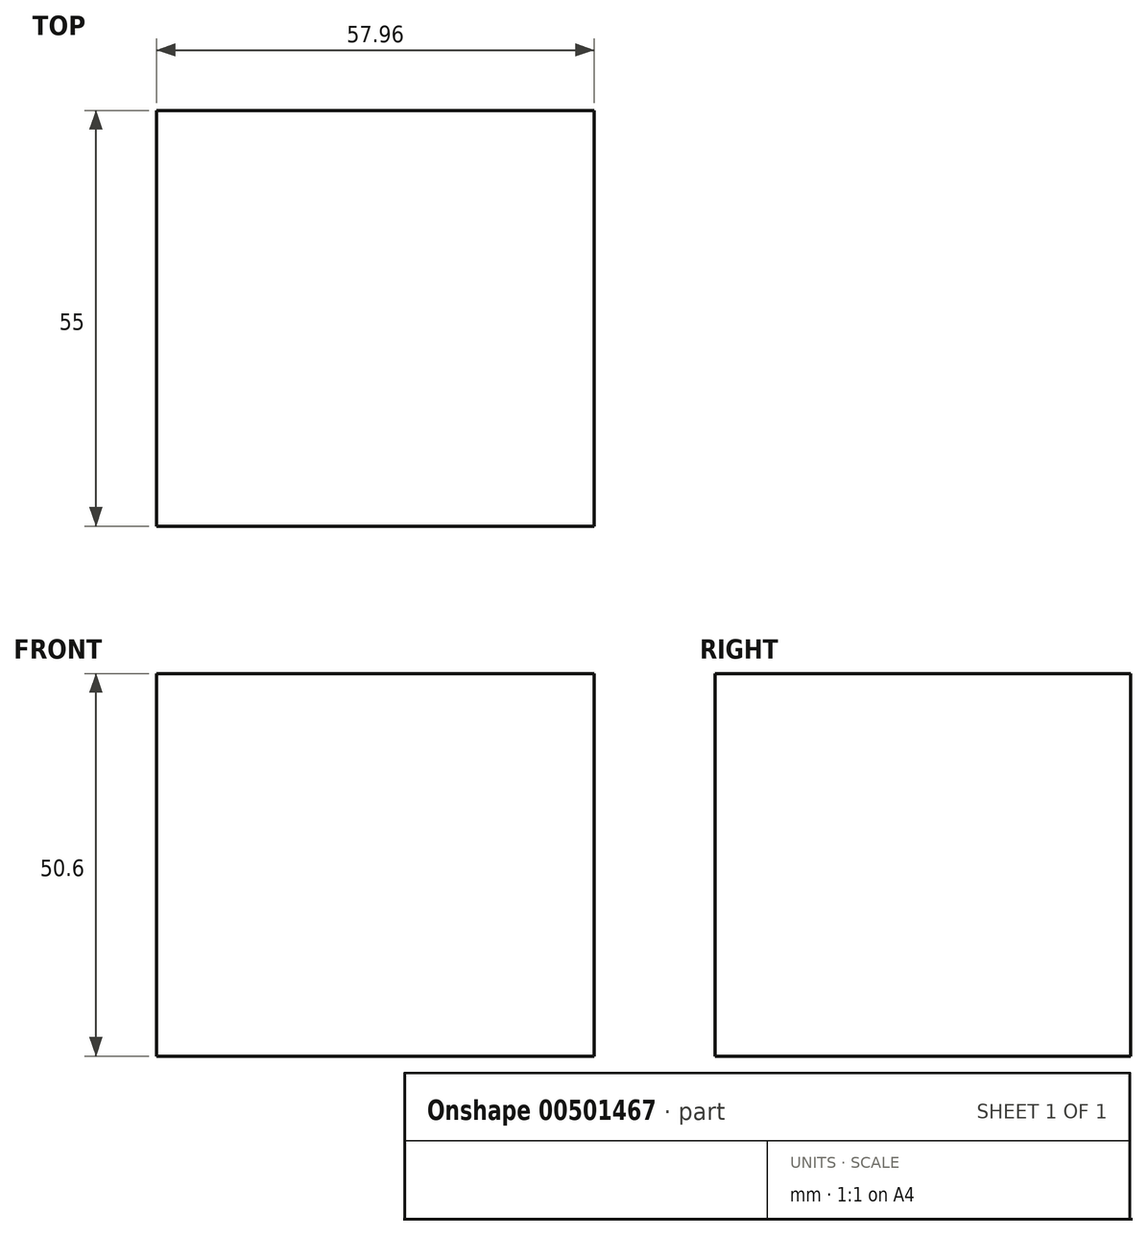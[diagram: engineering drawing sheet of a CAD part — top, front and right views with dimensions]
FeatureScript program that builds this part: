
annotation { "Feature Type Name" : "Feature", "Feature Type Description" : "" }
export const myFeature = defineFeature(function(context is Context, id is Id, definition is map)
    precondition{}
    {
        {
            var Q0;
            Q0=qCreatedBy(makeId("Front.planeOp"),FACE);
            var sketch = newSketch(context, id + "F0", { "sketchPlane" : qUnion([Q0])});
            skLineSegment(sketch, "E0", {"start": v(0, 0) * mm, "end": v(57.96, 0) * mm});
            skLineSegment(sketch, "E1", {"start": v(57.96, 0) * mm, "end": v(57.96, 50.6) * mm});
            skLineSegment(sketch, "E2", {"start": v(57.96, 50.6) * mm, "end": v(0, 50.6) * mm});
            skLineSegment(sketch, "E3", {"start": v(0, 50.6) * mm, "end": v(0, 0) * mm});
            skSolve(sketch);
        }
        {
            var Q0;
            Q0=makeQuery(id+"F0.imprint","IMPRINT",FACE,{"disambiguationData":[TD([[makeQuery(id+"F0.imprint","IMPRINT",EDGE,{"derivedFrom":sQuery(id+"F0.wireOp",EDGE,"E0")}),1.0]])]});
            extrude(context, id + "F1", {"entities" : qUnion([Q0]), "depth" : 55 * mm});
        }
    });
